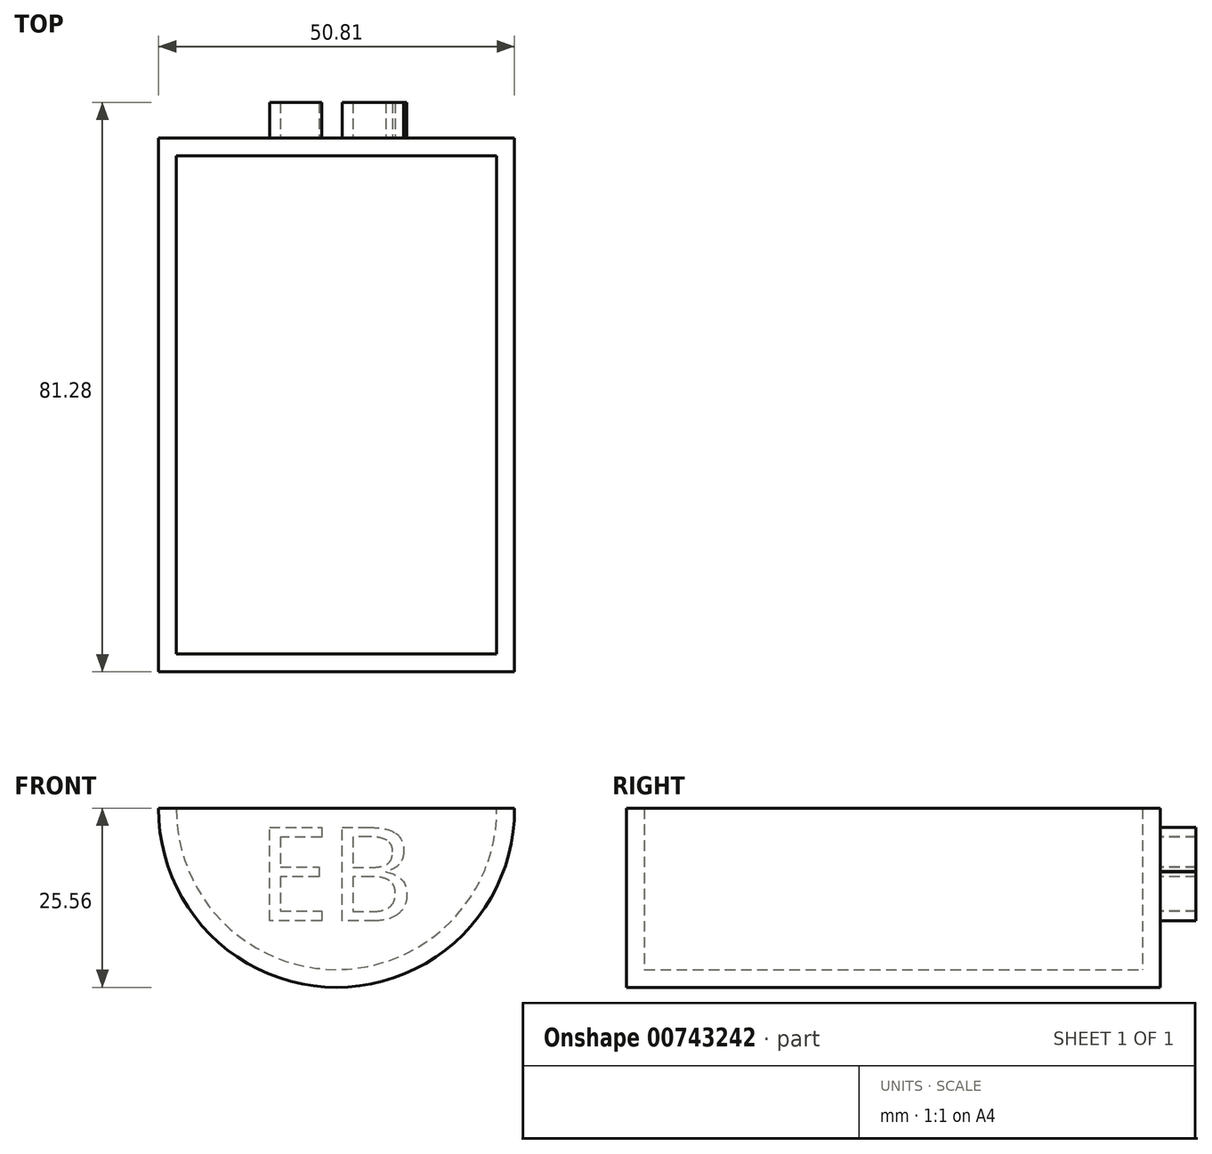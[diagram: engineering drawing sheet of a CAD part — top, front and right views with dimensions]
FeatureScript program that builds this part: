
annotation { "Feature Type Name" : "Feature", "Feature Type Description" : "" }
export const myFeature = defineFeature(function(context is Context, id is Id, definition is map)
    precondition{}
    {
        {
            var Q0;
            Q0=qCreatedBy(makeId("Front.planeOp"),FACE);
            var sketch = newSketch(context, id + "F0", { "sketchPlane" : qUnion([Q0])});
            skLineSegment(sketch, "E0", {"start": v(-65.56, 43.94) * mm, "end": v(-14.75, 43.94) * mm});
            skLineSegment(sketch, "E1", {"start": v(-40.15, 43.94) * mm, "end": v(-40.15, 18.54) * mm});
            skArc(sketch, "E2", {"start": v(-65.56, 43.94) * mm, "mid": v(-40.15, 18.38) * mm, "end": v(-14.75, 43.94) * mm});
            skSolve(sketch);
        }
        {
            var Q0;
            {var subQ0=sQuery(id+"F0.wireOp",EDGE,"E2");Q0=makeQuery(id+"F0.imprint","IMPRINT",FACE,{"disambiguationData":[TD([[makeQuery(id+"F0.imprint","IMPRINT",EDGE,{"derivedFrom":subQ0}),1.0]])]});}
            extrude(context, id + "F1", {"entities" : qUnion([Q0]), "depth" : 76.2 * mm, "offsetDistance" : 25.4 * mm});
        }
        {
            var Q0;
            Q0=makeQuery(id+"F1.opExtrude","SWEPT_FACE",FACE,{"disambiguationData":[OSD([sQuery(id+"F0.wireOp",EDGE,"E0")])]});
            shell(context, id + "F2", {"entities" : qUnion([Q0]), "thickness" : 2.54 * mm});
        }
        {
            var Q0;
            Q0=qCreatedBy(makeId("Front.planeOp"),FACE);
            var sketch = newSketch(context, id + "F3", { "sketchPlane" : qUnion([Q0])});
            skText(sketch, "E3", { "text": "EB\n", "fontName": "OpenSans-Regular.ttf"});
            const initialGuessF3  = {"E3": [-0.05154, 0.02789, 1, 0, 0.01343]};
            skSetInitialGuess(sketch, initialGuessF3);
            skSolve(sketch);
        }
        {
            var Q0;
            Q0 = qSketchRegion(id + "F3", true);
            extrude(context, id + "F4", {"entities" : qUnion([Q0]), "operationType" : NewBodyOperationType.ADD, "oppositeDirection" : true, "depth" : 5.08 * mm, "offsetDistance" : 25.4 * mm});
        }
    });
